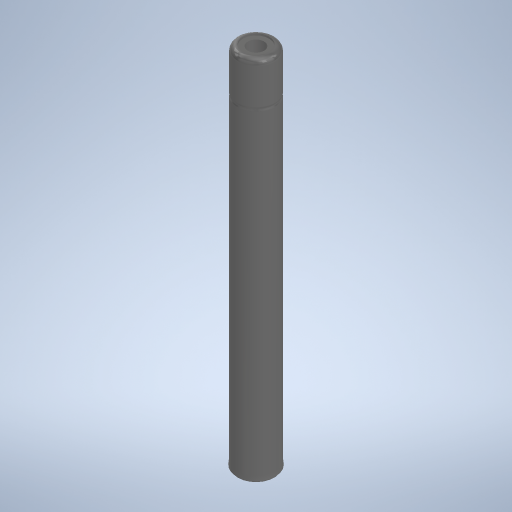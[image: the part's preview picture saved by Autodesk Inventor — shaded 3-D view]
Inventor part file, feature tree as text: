
AUTODESK INVENTOR PART (.ipt)
format: ipt  version: 2024 (Build 280153000, 153)  size: 289,792 bytes
history: native  units: mm
features: plane x1, split x1, direct_edit x1, boolean_combine x1, hole x1, sketch x1, other x1, move_body x1
ambient origin geometry x8: Origin, YZ Plane, XZ Plane, XY Plane, X Axis, Y Axis, Z Axis, Center Point
bodies: Solid1 (feature_tree), Solid2 (feature_tree), Solid3 (feature_tree)
feature tree (8):
  plane  "Work Plane1"
  split  "Split1"
  direct_edit  "Direct Edit2"
  boolean_combine  "Combine1"
  hole  "Hole1"  [1 undecoded]
  sketch  "Sketch1"  dims[d0=98.0mm d4=0.0mm d5=0.0mm d6=85.0mm d7=7.9mm d8=15.875mm d9=4.0mm d10=2.0mm d11=90.0deg d12=170.0mm d13=0.0mm]
  other  "Cut-Extrude1"
  move_body  "Move2"
note: 1 required parameter value undecoded (feature->parameter linkage not recoverable at this tier; creation-order binding heuristic only, values carry confidence <= 0.55)
